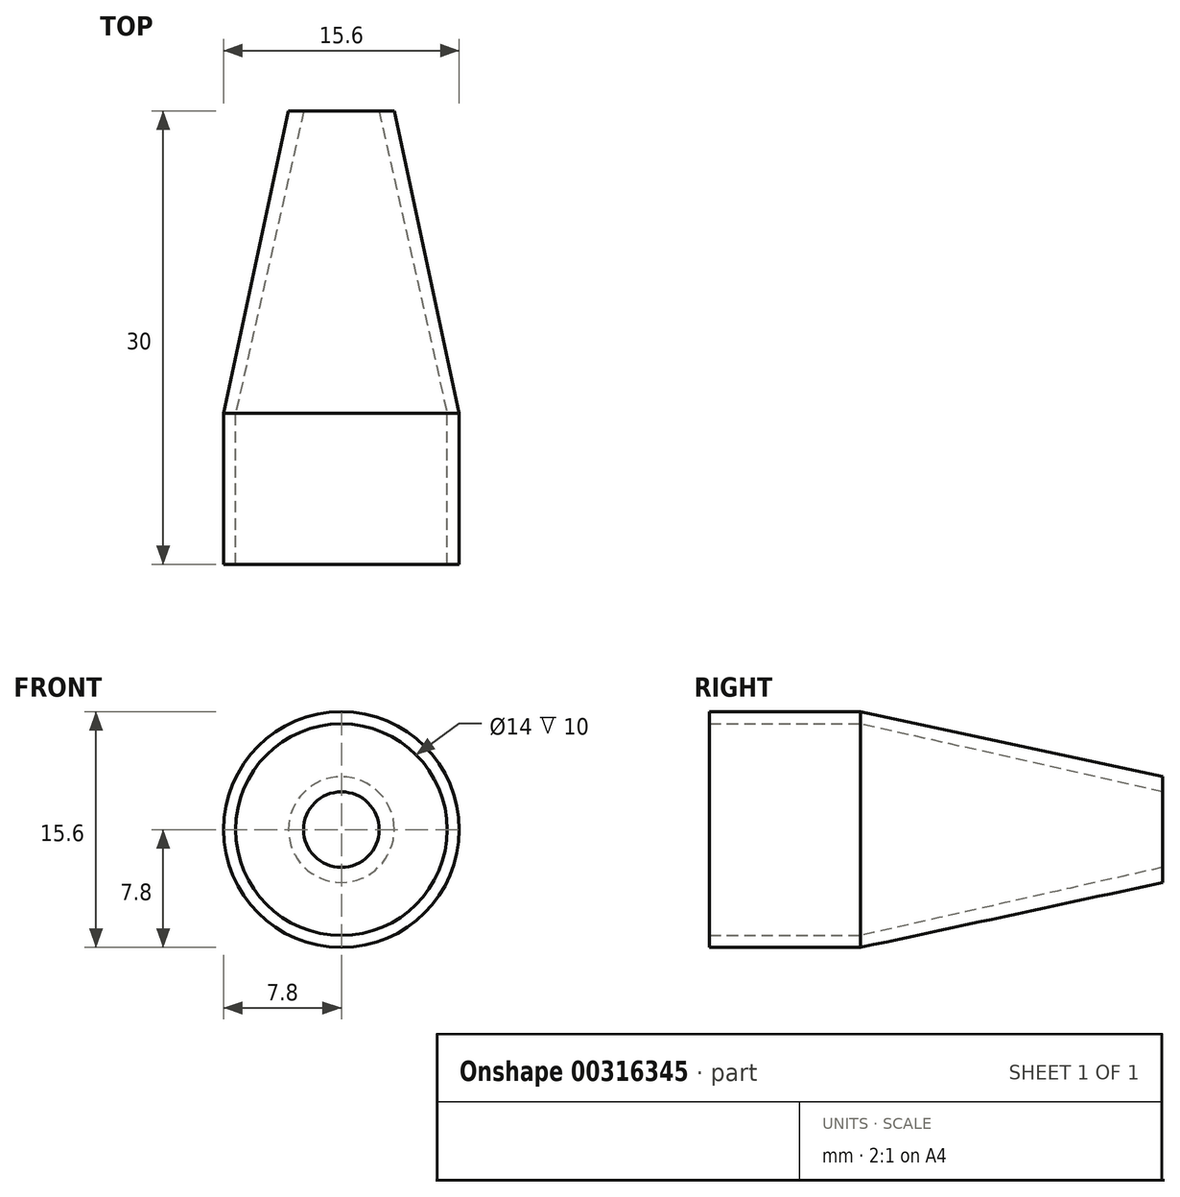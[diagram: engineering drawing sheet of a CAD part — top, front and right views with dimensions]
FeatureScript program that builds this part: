
annotation { "Feature Type Name" : "Feature", "Feature Type Description" : "" }
export const myFeature = defineFeature(function(context is Context, id is Id, definition is map)
    precondition{}
    {
        {
            var Q0;
            Q0=qCreatedBy(makeId("Front.planeOp"),FACE);
            cPlane(context, id + "F0", {"entities" : qUnion([Q0]), "cplaneType" : CPlaneType.OFFSET, "offset" : 20 * mm, "width" : 150 * mm, "height" : 150 * mm});
        }
        {
            var Q0;
            Q0=qCreatedBy(id+"F0.planeOp",FACE);
            var sketch = newSketch(context, id + "F1", { "sketchPlane" : qUnion([Q0])});
            skCircle(sketch, "E0", {"center": v(0, 0) * mm, "radius": 7.8 * mm});
            skSolve(sketch);
        }
        {
            var Q0;
            Q0=qCreatedBy(makeId("Front.planeOp"),FACE);
            var sketch = newSketch(context, id + "F2", { "sketchPlane" : qUnion([Q0])});
            skCircle(sketch, "E1", {"center": v(0, 0) * mm, "radius": 3.5 * mm});
            skSolve(sketch);
        }
        {
            var Q0;
            Q0=makeQuery(id+"F1.imprint","IMPRINT",FACE,{"disambiguationData":[TD([[makeQuery(id+"F1.imprint","IMPRINT",EDGE,{"derivedFrom":sQuery(id+"F1.wireOp",EDGE,"E0")}),1.0]])]});
            var Q1;
            Q1=makeQuery(id+"F2.imprint","IMPRINT",FACE,{"disambiguationData":[TD([[makeQuery(id+"F2.imprint","IMPRINT",EDGE,{"derivedFrom":sQuery(id+"F2.wireOp",EDGE,"E1")}),1.0]])]});
            loft(context, id + "F3", {"sheetProfilesArray" : [{ "sheetProfileEntities" : qUnion([Q0]) }, { "sheetProfileEntities" : qUnion([Q1]) }]});
        }
        {
            var Q0;
            Q0=makeQuery(id+"F3.opLoft","CAP_FACE",FACE,{"disambiguationData":[OSD([makeQuery(id+"F2.imprint","IMPRINT",FACE,{"disambiguationData":[TD([[makeQuery(id+"F2.imprint","IMPRINT",EDGE,{"derivedFrom":sQuery(id+"F2.wireOp",EDGE,"E1")}),1.0]])]})])],"isStart":true});
            var sketch = newSketch(context, id + "F4", { "sketchPlane" : qUnion([Q0])});
            skCircle(sketch, "E2", {"center": v(0, 0) * mm, "radius": 2.5 * mm});
            skSolve(sketch);
        }
        {
            var Q0;
            Q0=makeQuery(id+"F3.opLoft","CAP_FACE",FACE,{"disambiguationData":[OSD([makeQuery(id+"F1.imprint","IMPRINT",FACE,{"disambiguationData":[TD([[makeQuery(id+"F1.imprint","IMPRINT",EDGE,{"derivedFrom":sQuery(id+"F1.wireOp",EDGE,"E0")}),1.0]])]})])],"isStart":true});
            var sketch = newSketch(context, id + "F5", { "sketchPlane" : qUnion([Q0])});
            skCircle(sketch, "E3", {"center": v(0, 0) * mm, "radius": 7 * mm});
            skSolve(sketch);
        }
        {
            var Q1;
            Q1=makeQuery(id+"F5.imprint","IMPRINT",FACE,{"disambiguationData":[TD([[makeQuery(id+"F5.imprint","IMPRINT",EDGE,{"derivedFrom":sQuery(id+"F5.wireOp",EDGE,"E3")}),1.0]])]});
            var Q2;
            Q2=makeQuery(id+"F4.imprint","IMPRINT",FACE,{"disambiguationData":[TD([[makeQuery(id+"F4.imprint","IMPRINT",EDGE,{"derivedFrom":sQuery(id+"F4.wireOp",EDGE,"E2")}),1.0]])]});
            loft(context, id + "F6", {"operationType" : NewBodyOperationType.REMOVE, "sheetProfilesArray" : [{ "sheetProfileEntities" : qUnion([Q1]) }, { "sheetProfileEntities" : qUnion([Q2]) }]});
        }
        {
            var Q0;
            Q0=makeQuery(id+"F3.opLoft","CAP_FACE",FACE,{"disambiguationData":[OSD([makeQuery(id+"F1.imprint","IMPRINT",FACE,{"disambiguationData":[TD([[makeQuery(id+"F1.imprint","IMPRINT",EDGE,{"derivedFrom":sQuery(id+"F1.wireOp",EDGE,"E0")}),1.0]])]})])],"isStart":true});
            extrude(context, id + "F7", {"entities" : qUnion([Q0]), "operationType" : NewBodyOperationType.ADD, "depth" : 10 * mm});
        }
    });
